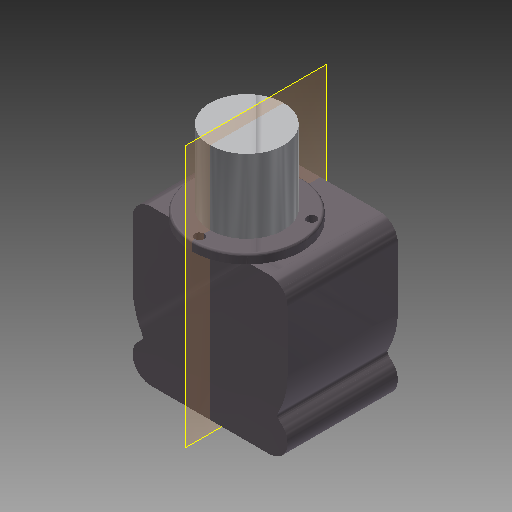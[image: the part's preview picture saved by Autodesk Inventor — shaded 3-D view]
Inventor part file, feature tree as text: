
AUTODESK INVENTOR PART (.ipt)
format: ipt  version: 2017 (Build 210142000, 142)  size: 192,000 bytes
history: native  units: in
note: dims shown in document units (in); Inventor stores cm internally (conversion verified against a paired STEP export)
features: sketch x5, extrude x4, fillet x3, reference x3, projected_geometry x2, hole x1
ambient origin geometry x8: Origin, YZ Plane, XZ Plane, XY Plane, X Axis, Y Axis, Z Axis, Center Point
bodies: Solid1 (feature_tree)
feature tree (18):
  extrude  "Extrusion1"  Depth=2.11in
  fillet  "Fillet1"  Radius=1.5in
  extrude  "Extrusion2"  Depth=0.5in
  fillet  "Fillet2"  Radius=0.5in
  extrude  "Extrusion3"  Depth=1.055in
  fillet  "Fillet3"  Radius=1.0in
  extrude  "Extrusion4"  Depth=1.5in
  hole  "Hole1"  [1 undecoded]
  sketch  "Sketch1"  dims[d0=2.11in d1=2.11in d2=1.5in d3=0.0in]
  sketch  "Sketch3"  dims[d4=0.25in d8=2.0in d9=0.5in]
  sketch  "Sketch4"  dims[d10=0.5in d12=1.055in d13=1.0in d14=0.0in]
  projected_geometry  "Projected Loop1"
  projected_geometry  "Projected Loop2"
  sketch  "Sketch5"  dims[d15=0.0625in d16=1.5in]
  sketch  "Sketch6"  dims[d17=0.25in d18=0.125in d19=0.0in d20=0.0312in d22=1.0in d23=0.0in d24=0.25in d25=0.129in d26=0.75in d27=0.225in d28=0.25in d29=0.5635in d30=0.25in d31=0.8108in]
  reference  "Reference1"
  reference  "Reference2"
  reference  "Reference3"
note: 1 required parameter value undecoded (feature->parameter linkage not recoverable at this tier; creation-order binding heuristic only, values carry confidence <= 0.55)
